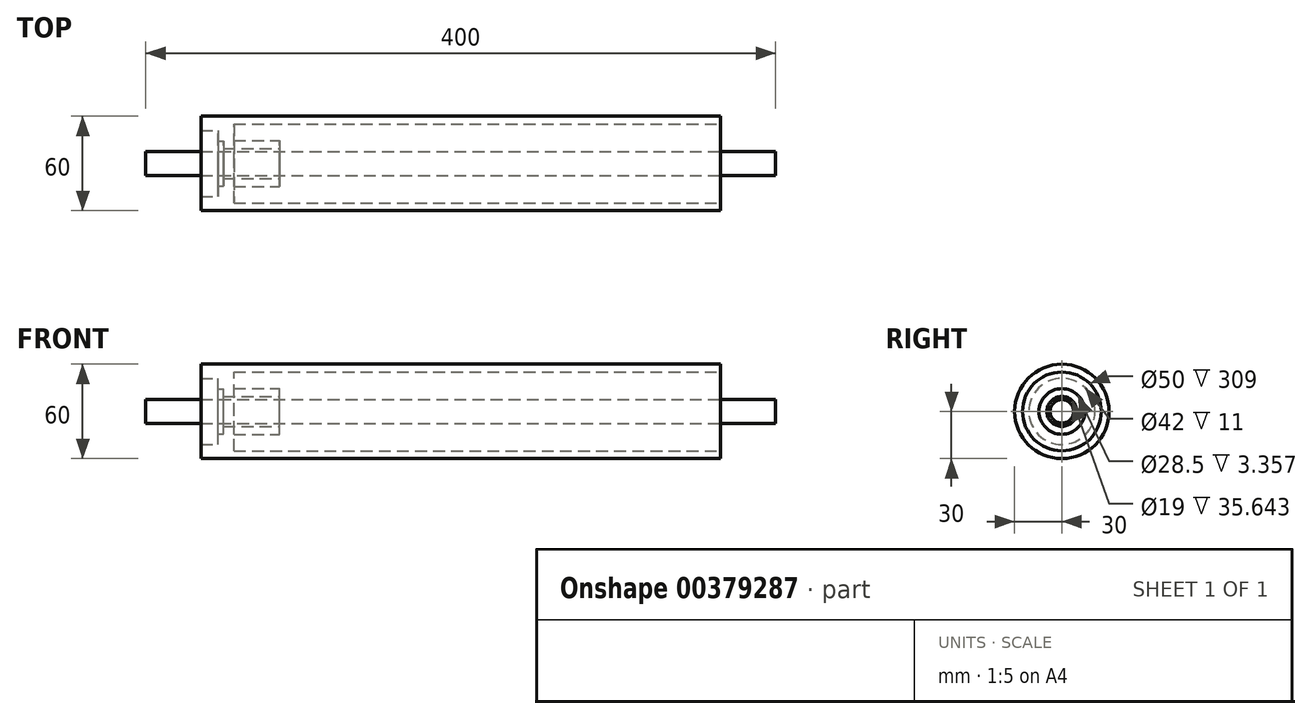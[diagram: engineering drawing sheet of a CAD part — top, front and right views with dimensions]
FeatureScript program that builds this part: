
annotation { "Feature Type Name" : "Feature", "Feature Type Description" : "" }
export const myFeature = defineFeature(function(context is Context, id is Id, definition is map)
    precondition{}
    {
        {
            var Q0;
            Q0=qCreatedBy(makeId("Front.planeOp"),FACE);
            var sketch = newSketch(context, id + "F0", { "sketchPlane" : qUnion([Q0])});
            skLineSegment(sketch, "E0.bottom", {"start": v(165, -30) * mm, "end": v(-165, -30) * mm});
            skLineSegment(sketch, "E0.top", {"start": v(165, 30) * mm, "end": v(-165, 30) * mm});
            skLineSegment(sketch, "E0.left", {"start": v(165, -30) * mm, "end": v(165, 30) * mm});
            skLineSegment(sketch, "E0.right", {"start": v(-165, -30) * mm, "end": v(-165, 30) * mm});
            skPoint(sketch, "E0.middle", {"position": v(0, 0) * mm});
            skLineSegment(sketch, "E1", {"start": v(-165, 25) * mm, "end": v(165, 25) * mm});
            skLineSegment(sketch, "E2", {"start": v(-178.87, 0) * mm, "end": v(193.67, 0) * mm, "construction": true});
            skPoint(sketch, "E2.endSnap0", {"position": v(165, 0) * mm});
            skLineSegment(sketch, "E3", {"start": v(-200, 7.5) * mm, "end": v(200, 7.5) * mm});
            skLineSegment(sketch, "E4", {"start": v(200, 7.5) * mm, "end": v(200, 0) * mm});
            skLineSegment(sketch, "E5", {"start": v(200, 0) * mm, "end": v(-200, 0) * mm});
            skLineSegment(sketch, "E6", {"start": v(-200, 0) * mm, "end": v(-200, 7.5) * mm});
            skLineSegment(sketch, "E7", {"start": v(-165, 21) * mm, "end": v(-154, 21) * mm});
            skLineSegment(sketch, "E8", {"start": v(-154, 21) * mm, "end": v(-154, -21) * mm});
            skLineSegment(sketch, "E9", {"start": v(-154, -21) * mm, "end": v(-165, -21) * mm});
            skLineSegment(sketch, "E10", {"start": v(-144, 25) * mm, "end": v(-144, 14.5) * mm});
            skLineSegment(sketch, "E11", {"start": v(-144, 14.5) * mm, "end": v(-115, 14.5) * mm});
            skLineSegment(sketch, "E12", {"start": v(-115, 14.5) * mm, "end": v(-115, 9.5) * mm});
            skLineSegment(sketch, "E13", {"start": v(-115, 9.5) * mm, "end": v(-150.64, 9.5) * mm});
            skLineSegment(sketch, "E14", {"start": v(-154, 14.25) * mm, "end": v(-150.64, 14.25) * mm});
            skLineSegment(sketch, "E15", {"start": v(-150.64, 14.25) * mm, "end": v(-150.64, 0) * mm});
            skSolve(sketch);
        }
        {
            var Q0;
            {var subQ4=sQuery(id+"F0.wireOp",EDGE,"E0.top");Q0=makeQuery(id+"F0.imprint","IMPRINT",FACE,{"disambiguationData":[TD([[makeQuery(id+"F0.imprint","IMPRINT",EDGE,{"derivedFrom":subQ4}),1.0]])]});}
            var Q1;
            Q1=sQuery(id+"F0.wireOp",EDGE,"E5");
            revolve(context, id + "F1", {"entities" : qUnion([Q0]), "axis" : qUnion([Q1]), "revolveType" : RevolveType.FULL});
        }
        {
            var Q0;
            {var subQ0=sQuery(id+"F0.wireOp",EDGE,"E7");Q0=makeQuery(id+"F0.imprint","IMPRINT",FACE,{"disambiguationData":[TD([[makeQuery(id+"F0.imprint","IMPRINT",EDGE,{"derivedFrom":subQ0}),1.0]])]});}
            var Q1;
            Q1=sQuery(id+"F0.wireOp",EDGE,"E5");
            revolve(context, id + "F2", {"operationType" : NewBodyOperationType.ADD, "entities" : qUnion([Q0]), "axis" : qUnion([Q1]), "revolveType" : RevolveType.FULL});
        }
        {
            var Q0;
            {var subQ0=sQuery(id+"F0.wireOp",EDGE,"E5");var subQ1=sQuery(id+"F0.wireOp",EDGE,"E0.left");var subQ2=makeQuery(id+"F0.imprint","INTERSECT",VERTEX,{"derivedFrom":[subQ1,subQ0]});Q0=makeQuery(id+"F0.imprint","IMPRINT",FACE,{"disambiguationData":[TD([[makeQuery(id+"F0.imprint","IMPRINT",EDGE,{"disambiguationData":[TD([[subQ2,-1.0]])],"derivedFrom":subQ1}),1.0]])]});}
            var Q1;
            {var subQ0=sQuery(id+"F0.wireOp",EDGE,"E5");var subQ1=sQuery(id+"F0.wireOp",EDGE,"E0.right");var subQ2=makeQuery(id+"F0.imprint","INTERSECT",VERTEX,{"derivedFrom":[subQ1,subQ0]});Q1=makeQuery(id+"F0.imprint","IMPRINT",FACE,{"disambiguationData":[TD([[makeQuery(id+"F0.imprint","IMPRINT",EDGE,{"disambiguationData":[TD([[subQ2,-1.0]])],"derivedFrom":subQ1}),-1.0]])]});}
            var Q2;
            {var subQ0=sQuery(id+"F0.wireOp",EDGE,"E8");var subQ1=sQuery(id+"F0.wireOp",EDGE,"E3");var subQ2=makeQuery(id+"F0.imprint","INTERSECT",VERTEX,{"derivedFrom":[subQ1,subQ0]});Q2=makeQuery(id+"F0.imprint","IMPRINT",FACE,{"disambiguationData":[TD([[makeQuery(id+"F0.imprint","IMPRINT",EDGE,{"disambiguationData":[TD([[subQ2,-1.0]])],"derivedFrom":subQ1}),-1.0]])]});}
            var Q3;
            {var subQ5=sQuery(id+"F0.wireOp",EDGE,"E6");Q3=makeQuery(id+"F0.imprint","IMPRINT",FACE,{"disambiguationData":[TD([[makeQuery(id+"F0.imprint","IMPRINT",EDGE,{"derivedFrom":subQ5}),-1.0]])]});}
            var Q4;
            {var subQ5=sQuery(id+"F0.wireOp",EDGE,"E4");Q4=makeQuery(id+"F0.imprint","IMPRINT",FACE,{"disambiguationData":[TD([[makeQuery(id+"F0.imprint","IMPRINT",EDGE,{"derivedFrom":subQ5}),-1.0]])]});}
            var Q5;
            Q5=sQuery(id+"F0.wireOp",EDGE,"E5");
            revolve(context, id + "F3", {"entities" : qUnion([Q0, Q1, Q2, Q3, Q4]), "axis" : qUnion([Q5]), "revolveType" : RevolveType.FULL});
        }
    });
